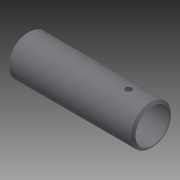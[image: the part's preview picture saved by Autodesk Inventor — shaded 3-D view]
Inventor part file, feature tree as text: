
AUTODESK INVENTOR PART (.ipt)
format: ipt  version: 2014 (Build 180170000, 170)  size: 136,704 bytes
history: native  units: in
note: dims shown in document units (in); Inventor stores cm internally (conversion verified against a paired STEP export)
features: other x56, revolve x2, sketch x2
ambient origin geometry x8: Origin, YZ Plane, XZ Plane, XY Plane, X Axis, Y Axis, Z Axis, Center Point
bodies: Solid1 (feature_tree)
feature tree (60):
  revolve  "Revolution1"  Angle=360.0deg
  revolve  "Revolution2"  [1 undecoded]
  other  "o1_XY"
  other  "o1_YZ"
  other  "o1_ZX"
  other  "o1_X"
  other  "o1_Y"
  other  "o1_Z"
  other  "o1_Center"
  other  "o2_XY"
  other  "o2_YZ"
  other  "o2_ZX"
  other  "o2_X"
  other  "o2_Y"
  other  "o2_Z"
  other  "o2_Center"
  other  "t1_XY"
  other  "t1_YZ"
  other  "t1_ZX"
  other  "t1_X"
  other  "t1_Y"
  other  "t1_Z"
  other  "t1_Center"
  other  "t2_XY"
  other  "t2_YZ"
  other  "t2_ZX"
  other  "t2_X"
  other  "t2_Y"
  other  "t2_Z"
  other  "t2_Center"
  other  "t3_XY"
  other  "t3_YZ"
  other  "t3_ZX"
  other  "t3_X"
  other  "t3_Y"
  other  "t3_Z"
  other  "t3_Center"
  other  "t4_XY"
  other  "t4_YZ"
  other  "t4_ZX"
  other  "t4_X"
  other  "t4_Y"
  other  "t4_Z"
  other  "t4_Center"
  other  "tube1_XY"
  other  "tube1_YZ"
  other  "tube1_ZX"
  other  "tube1_X"
  other  "tube1_Y"
  other  "tube1_Z"
  other  "tube1_Center"
  other  "tube2_XY"
  other  "tube2_YZ"
  other  "tube2_ZX"
  other  "tube2_X"
  other  "tube2_Y"
  other  "tube2_Z"
  other  "tube2_Center"
  sketch  "Sketch_5"
  sketch  "Sketch_1"  dims[d0=360.0deg d1=360.0deg]
note: 1 required parameter value undecoded (feature->parameter linkage not recoverable at this tier; creation-order binding heuristic only, values carry confidence <= 0.55)
